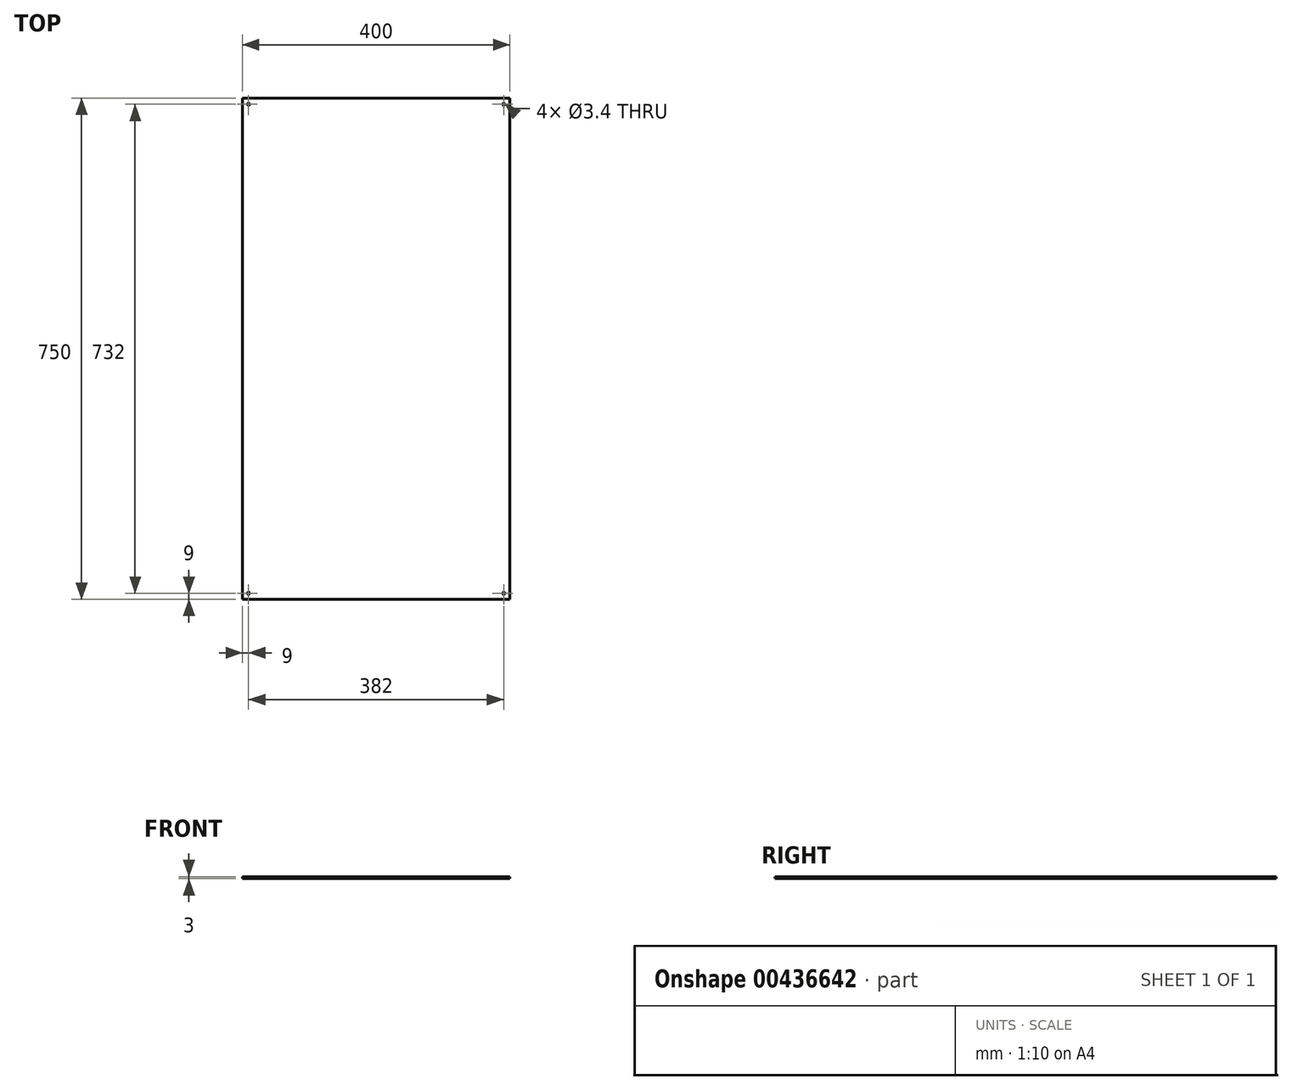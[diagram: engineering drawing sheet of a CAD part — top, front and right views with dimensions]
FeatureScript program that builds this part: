
annotation { "Feature Type Name" : "Feature", "Feature Type Description" : "" }
export const myFeature = defineFeature(function(context is Context, id is Id, definition is map)
    precondition{}
    {
        {
            var Q0;
            Q0=qCreatedBy(makeId("Top.planeOp"),FACE);
            var sketch = newSketch(context, id + "F0", { "sketchPlane" : qUnion([Q0])});
            skLineSegment(sketch, "E0.bottom", {"start": v(200, 375) * mm, "end": v(-200, 375) * mm});
            skLineSegment(sketch, "E0.top", {"start": v(200, -375) * mm, "end": v(-200, -375) * mm});
            skLineSegment(sketch, "E0.left", {"start": v(200, 375) * mm, "end": v(200, -375) * mm});
            skLineSegment(sketch, "E0.right", {"start": v(-200, 375) * mm, "end": v(-200, -375) * mm});
            skPoint(sketch, "E0.middle", {"position": v(0, 0) * mm});
            skLineSegment(sketch, "E1", {"start": v(-191, 375) * mm, "end": v(-191, 366) * mm, "construction": true});
            skLineSegment(sketch, "E2", {"start": v(-191, 366) * mm, "end": v(-200, 366) * mm, "construction": true});
            skCircle(sketch, "E3", {"center": v(-191, 366) * mm, "radius": 1.7 * mm});
            skLineSegment(sketch, "E4", {"start": v(191, 375) * mm, "end": v(191, 366) * mm, "construction": true});
            skLineSegment(sketch, "E5", {"start": v(191, 366) * mm, "end": v(200, 366) * mm, "construction": true});
            skCircle(sketch, "E6", {"center": v(191, 366) * mm, "radius": 1.7 * mm});
            skLineSegment(sketch, "E7", {"start": v(-200, -366) * mm, "end": v(-191, -366) * mm, "construction": true});
            skLineSegment(sketch, "E8", {"start": v(-191, -366) * mm, "end": v(-191, -375) * mm, "construction": true});
            skCircle(sketch, "E9", {"center": v(-191, -366) * mm, "radius": 1.7 * mm});
            skLineSegment(sketch, "E10", {"start": v(200, -366) * mm, "end": v(191, -366) * mm, "construction": true});
            skLineSegment(sketch, "E11", {"start": v(191, -366) * mm, "end": v(191, -375) * mm, "construction": true});
            skCircle(sketch, "E12", {"center": v(191, -366) * mm, "radius": 1.7 * mm});
            skSolve(sketch);
        }
        {
            var Q0;
            Q0=makeQuery(id+"F0.imprint","IMPRINT",FACE,{"disambiguationData":[TD([[makeQuery(id+"F0.imprint","IMPRINT",EDGE,{"derivedFrom":sQuery(id+"F0.wireOp",EDGE,"E0.bottom")}),1.0]])]});
            extrude(context, id + "F1", {"entities" : qUnion([Q0]), "depth" : 3 * mm});
        }
    });
